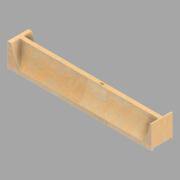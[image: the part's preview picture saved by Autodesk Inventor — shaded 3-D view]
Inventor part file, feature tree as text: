
AUTODESK INVENTOR PART (.ipt)
format: ipt  version: 2022.2 (Build 262287010, 287A)  size: 165,376 bytes
history: native  units: in
note: dims shown in document units (in); Inventor stores cm internally (conversion verified against a paired STEP export)
features: plane x1, extrude x1, sketch x1, other x1
ambient origin geometry x8: Origin, YZ Plane, XZ Plane, XY Plane, X Axis, Y Axis, Z Axis, Center Point
bodies: Solid1 (feature_tree)
feature tree (4):
  plane  "Work Plane1"
  extrude  "Extrusion1"  Depth=8.75in
  sketch  "Sketch1"  dims[d1=8.75in d2=8.75in d3=35.4375in d4=0.0in]
  other  "North (6)"
